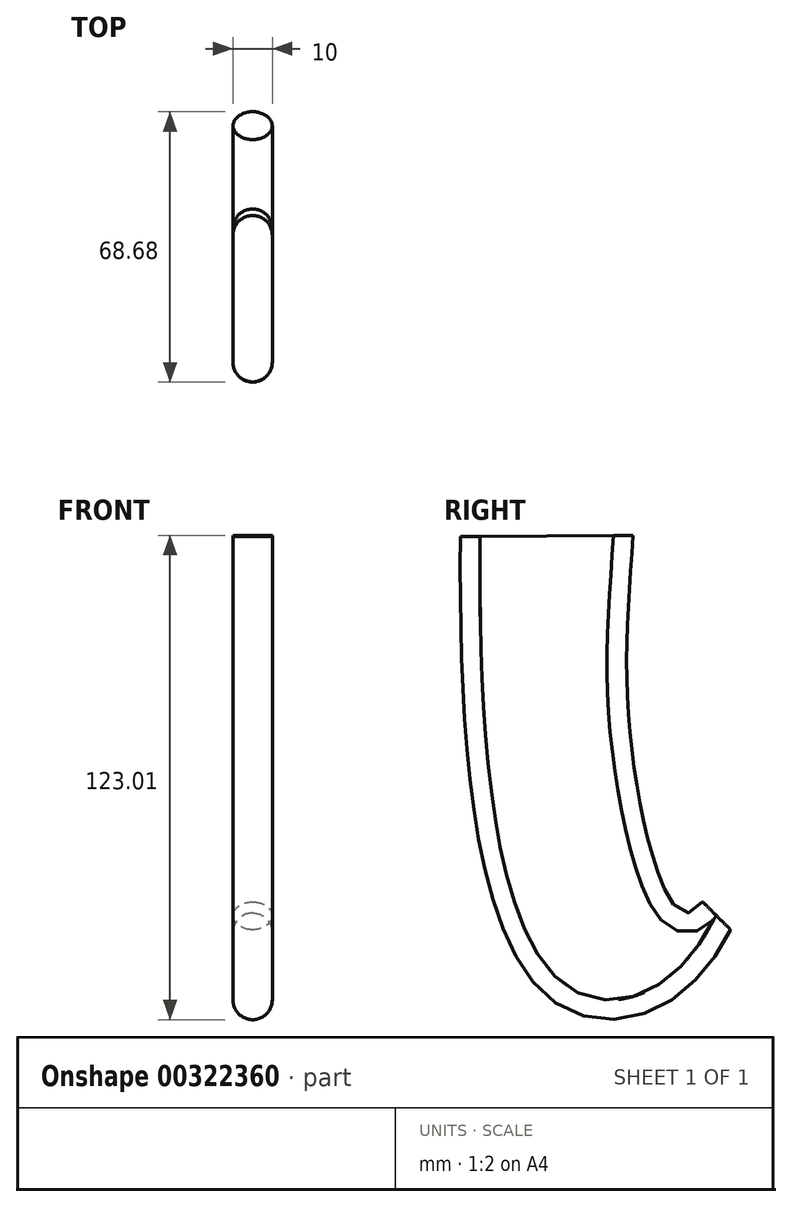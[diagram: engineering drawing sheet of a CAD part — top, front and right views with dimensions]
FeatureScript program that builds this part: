
annotation { "Feature Type Name" : "Feature", "Feature Type Description" : "" }
export const myFeature = defineFeature(function(context is Context, id is Id, definition is map)
    precondition{}
    {
        {
            var Q0;
            Q0=qCreatedBy(makeId("Top.planeOp"),FACE);
            var sketch = newSketch(context, id + "F0", { "sketchPlane" : qUnion([Q0])});
            skLineSegment(sketch, "E0.bottom", {"start": v(50, 50) * mm, "end": v(-50, 50) * mm});
            skLineSegment(sketch, "E0.top", {"start": v(50, -50) * mm, "end": v(-50, -50) * mm});
            skLineSegment(sketch, "E0.left", {"start": v(50, 50) * mm, "end": v(50, -50) * mm});
            skLineSegment(sketch, "E0.right", {"start": v(-50, 50) * mm, "end": v(-50, -50) * mm});
            skPoint(sketch, "E0.middle", {"position": v(0, 0) * mm});
            skSolve(sketch);
        }
        {
            var Q0;
            Q0=qCreatedBy(makeId("Right.planeOp"),FACE);
            var sketch = newSketch(context, id + "F1", { "sketchPlane" : qUnion([Q0])});
            skLineSegment(sketch, "E1", {"start": v(32.93, -92.93) * mm, "end": v(40, -100) * mm});
            skLineSegment(sketch, "E2", {"start": v(40, -100) * mm, "end": v(50, -100) * mm});
            skLineSegment(sketch, "E3", {"start": v(50, -100) * mm, "end": v(50, 0) * mm});
            skFitSpline(sketch, "E4", {"points": [v(32.93, -92.93) * mm, v(15.85, -60.9) * mm, v(15.28, 0.16) * mm], "startDerivative": vector(-52.88, -76.34) * mm, "endDerivative": vector(6.5, 101.97) * mm});
            skFitSpline(sketch, "E5", {"points": [v(40, -100) * mm, v(-2.64, -119.7) * mm, v(-28.64, -0.08) * mm], "startDerivative": vector(-85.75, -170.07) * mm, "endDerivative": vector(2.63, 300.67) * mm});
            skLineSegment(sketch, "E6", {"start": v(15.28, 0.16) * mm, "end": v(-28.64, -0.08) * mm});
            skSolve(sketch);
        }
        {
            var Q0;
            Q0=makeQuery(id+"F1.imprint","IMPRINT",FACE,{"disambiguationData":[TD([[makeQuery(id+"F1.imprint","IMPRINT",EDGE,{"derivedFrom":sQuery(id+"F1.wireOp",EDGE,"E1")}),-1.0]])]});
            extrude(context, id + "F2", {"entities" : qUnion([Q0]), "endBound" : BoundingType.SYMMETRIC, "depth" : 10 * mm});
        }
        {
            var Q0;
            Q0=makeQuery(id+"F2.opExtrude","CAP_EDGE",EDGE,{"disambiguationData":[OSD([sQuery(id+"F1.wireOp",EDGE,"E4")])],"isStart":false});
            var Q1;
            Q1=makeQuery(id+"F2.opExtrude","CAP_EDGE",EDGE,{"disambiguationData":[OSD([sQuery(id+"F1.wireOp",EDGE,"E5")])],"isStart":false});
            var Q2;
            Q2=makeQuery(id+"F2.opExtrude","CAP_EDGE",EDGE,{"disambiguationData":[OSD([sQuery(id+"F1.wireOp",EDGE,"E4")])],"isStart":true});
            var Q3;
            Q3=makeQuery(id+"F2.opExtrude","CAP_EDGE",EDGE,{"disambiguationData":[OSD([sQuery(id+"F1.wireOp",EDGE,"E5")])],"isStart":true});
            fillet(context, id + "F3", {"entities" : qUnion([Q0, Q1, Q2, Q3]), "radius" : 5 * mm, "tangentPropagation" : true, "allowEdgeOverflow" : false});
        }
    });
